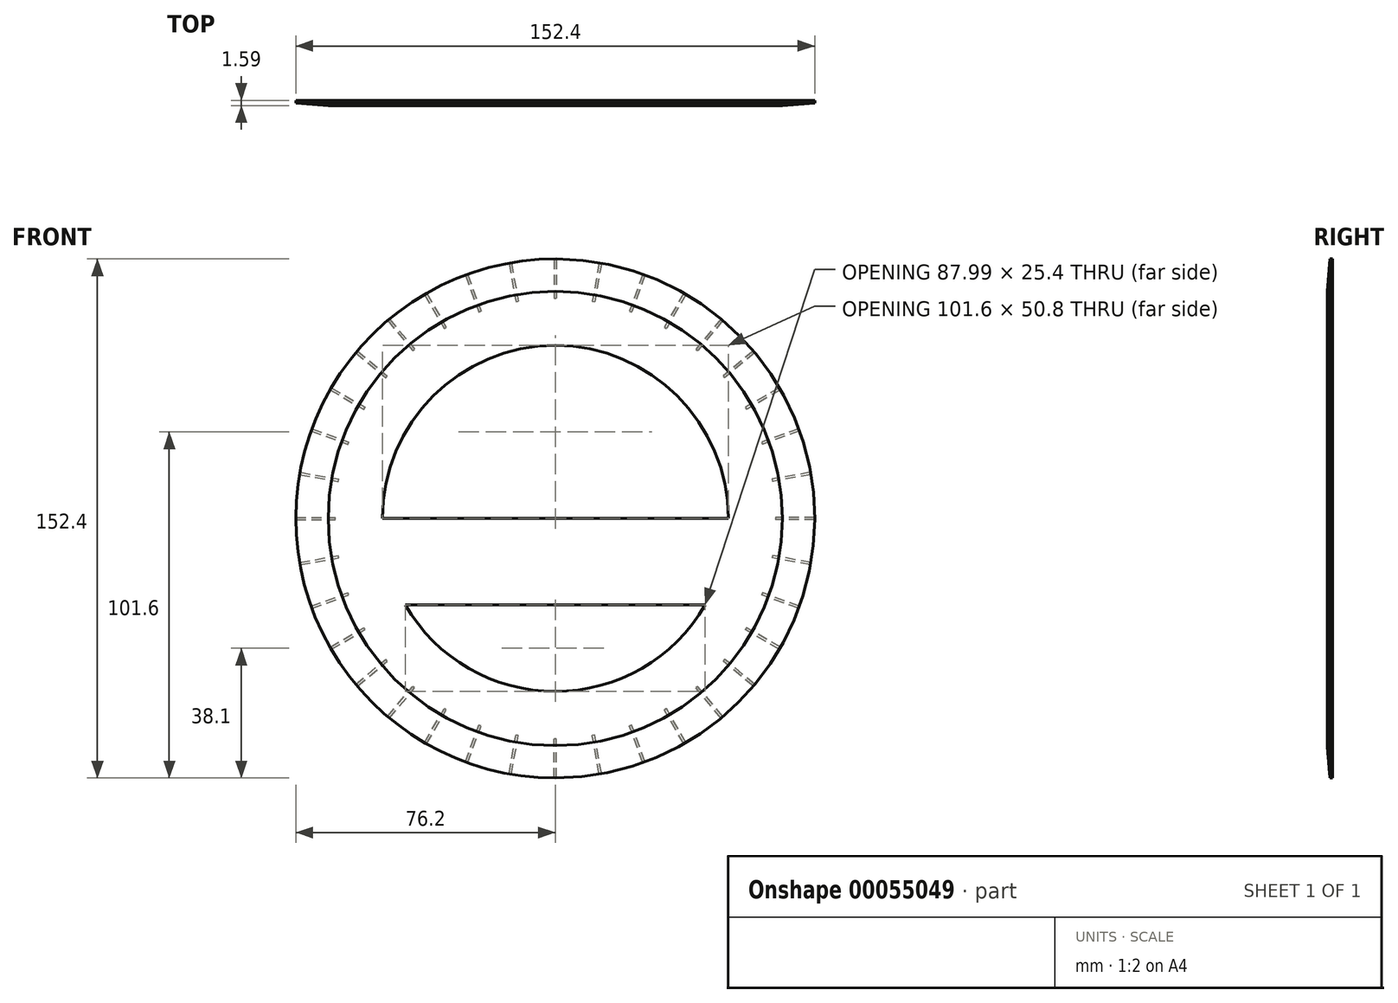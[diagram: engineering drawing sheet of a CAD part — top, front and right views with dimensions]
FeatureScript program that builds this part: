
annotation { "Feature Type Name" : "Feature", "Feature Type Description" : "" }
export const myFeature = defineFeature(function(context is Context, id is Id, definition is map)
    precondition{}
    {
        {
            var Q0;
            Q0=qCreatedBy(makeId("Front.planeOp"),FACE);
            var sketch = newSketch(context, id + "F0", { "sketchPlane" : qUnion([Q0])});
            skCircle(sketch, "E0", {"center": v(0, 0) * mm, "radius": 76.2 * mm});
            skCircle(sketch, "E1", {"center": v(0, 0) * mm, "radius": 50.8 * mm});
            skLineSegment(sketch, "E2", {"start": v(-50.8, 0) * mm, "end": v(50.8, 0) * mm});
            skLineSegment(sketch, "E3", {"start": v(-44, -25.4) * mm, "end": v(44, -25.4) * mm});
            skSolve(sketch);
        }
        {
            var Q0;
            Q0=makeQuery(id+"F0.imprint","IMPRINT",FACE,{"disambiguationData":[TD([[makeQuery(id+"F0.imprint","IMPRINT",EDGE,{"derivedFrom":sQuery(id+"F0.wireOp",EDGE,"E0")}),1.0]])]});
            var Q1;
            {var subQ0=sQuery(id+"F0.wireOp",EDGE,"E2");Q1=makeQuery(id+"F0.imprint","IMPRINT",FACE,{"disambiguationData":[TD([[makeQuery(id+"F0.imprint","IMPRINT",EDGE,{"derivedFrom":subQ0}),-1.0]])]});}
            extrude(context, id + "F1", {"entities" : qUnion([Q0, Q1]), "depth" : 1.59 * mm});
        }
        {
            var Q0;
            Q0=qCreatedBy(makeId("Top.planeOp"),FACE);
            var sketch = newSketch(context, id + "F2", { "sketchPlane" : qUnion([Q0])});
            skLineSegment(sketch, "E4", {"start": v(76.2, 0) * mm, "end": v(76.2, -1.59) * mm, "construction": true});
            skLineSegment(sketch, "E5.0", {"start": v(76.2, -1.59) * mm, "end": v(-76.2, -1.59) * mm, "construction": true});
            skLineSegment(sketch, "E6", {"start": v(76.2, -0.8) * mm, "end": v(66.67, -1.59) * mm});
            skLineSegment(sketch, "E7", {"start": v(66.67, -1.59) * mm, "end": v(76.2, -1.59) * mm});
            skLineSegment(sketch, "E8", {"start": v(0, 17.15) * mm, "end": v(0, -24.9) * mm, "construction": true});
            skLineSegment(sketch, "E9", {"start": v(76.2, -0.8) * mm, "end": v(76.2, -1.59) * mm});
            skSolve(sketch);
        }
        {
            var Q0;
            Q0=makeQuery(id+"F2.imprint","IMPRINT",FACE,{"disambiguationData":[TD([[makeQuery(id+"F2.imprint","IMPRINT",EDGE,{"derivedFrom":sQuery(id+"F2.wireOp",EDGE,"E6")}),1.0]])]});
            var Q1;
            Q1=sQuery(id+"F2.wireOp",EDGE,"E9");
            var Q2;
            Q2=sQuery(id+"F2.wireOp",EDGE,"E6");
            var Q3;
            Q3=sQuery(id+"F2.wireOp",EDGE,"E7");
            var Q4;
            Q4=sQuery(id+"F2.wireOp",EDGE,"E8");
            revolve(context, id + "F3", {"operationType" : NewBodyOperationType.REMOVE, "entities" : qUnion([Q0]), "surfaceEntities" : qUnion([Q1, Q2, Q3]), "axis" : qUnion([Q4]), "revolveType" : RevolveType.FULL, "oppositeDirection" : true});
        }
        {
            var Q0;
            Q0=makeQuery(id+"F1.opExtrude","CAP_FACE",FACE,{"disambiguationData":[OSD([sQuery(id+"F0.wireOp",EDGE,"E0"),sQuery(id+"F0.wireOp",EDGE,"E1"),sQuery(id+"F0.wireOp",EDGE,"E2"),sQuery(id+"F0.wireOp",EDGE,"E3")])],"isStart":true});
            var sketch = newSketch(context, id + "F4", { "sketchPlane" : qUnion([Q0])});
            skLineSegment(sketch, "E10.rect.bottom", {"start": v(76.2, -0.35) * mm, "end": v(64.66, -0.35) * mm});
            skLineSegment(sketch, "E10.rect.top", {"start": v(76.2, 0.35) * mm, "end": v(64.66, 0.35) * mm});
            skLineSegment(sketch, "E10.rect.left", {"start": v(76.2, -0.35) * mm, "end": v(76.2, 0.35) * mm});
            skLineSegment(sketch, "E10.rect.right", {"start": v(64.66, -0.35) * mm, "end": v(64.66, 0.35) * mm});
            skPoint(sketch, "E10.rect.middle", {"position": v(70.43, 0) * mm});
            skLineSegment(sketch, "E11.1.0", {"start": v(75.1, 12.9) * mm, "end": v(63.74, 10.89) * mm});
            skLineSegment(sketch, "E11.1.1", {"start": v(74.98, 13.57) * mm, "end": v(63.62, 11.57) * mm});
            skPoint(sketch, "E11.1.2", {"position": v(69.36, 12.23) * mm});
            skLineSegment(sketch, "E11.1.3", {"start": v(75.1, 12.9) * mm, "end": v(74.98, 13.57) * mm});
            skLineSegment(sketch, "E11.1.4", {"start": v(63.74, 10.89) * mm, "end": v(63.62, 11.57) * mm});
            skLineSegment(sketch, "E11.2.0", {"start": v(71.72, 25.74) * mm, "end": v(60.88, 21.8) * mm});
            skLineSegment(sketch, "E11.2.1", {"start": v(71.49, 26.39) * mm, "end": v(60.65, 22.44) * mm});
            skPoint(sketch, "E11.2.2", {"position": v(66.18, 24.09) * mm});
            skLineSegment(sketch, "E11.2.3", {"start": v(71.72, 25.74) * mm, "end": v(71.49, 26.39) * mm});
            skLineSegment(sketch, "E11.2.4", {"start": v(60.88, 21.8) * mm, "end": v(60.65, 22.44) * mm});
            skLineSegment(sketch, "E11.3.0", {"start": v(66.16, 37.8) * mm, "end": v(56.17, 32.03) * mm});
            skLineSegment(sketch, "E11.3.1", {"start": v(65.82, 38.4) * mm, "end": v(55.83, 32.63) * mm});
            skPoint(sketch, "E11.3.2", {"position": v(61, 35.22) * mm});
            skLineSegment(sketch, "E11.3.3", {"start": v(66.16, 37.8) * mm, "end": v(65.82, 38.4) * mm});
            skLineSegment(sketch, "E11.3.4", {"start": v(56.17, 32.03) * mm, "end": v(55.83, 32.63) * mm});
            skLineSegment(sketch, "E11.4.0", {"start": v(58.6, 48.71) * mm, "end": v(49.76, 41.3) * mm});
            skLineSegment(sketch, "E11.4.1", {"start": v(58.15, 49.25) * mm, "end": v(49.31, 41.83) * mm});
            skPoint(sketch, "E11.4.2", {"position": v(53.95, 45.27) * mm});
            skLineSegment(sketch, "E11.4.3", {"start": v(58.6, 48.71) * mm, "end": v(58.15, 49.25) * mm});
            skLineSegment(sketch, "E11.4.4", {"start": v(49.76, 41.3) * mm, "end": v(49.31, 41.83) * mm});
            skLineSegment(sketch, "E11.5.0", {"start": v(49.25, 58.15) * mm, "end": v(41.83, 49.31) * mm});
            skLineSegment(sketch, "E11.5.1", {"start": v(48.71, 58.6) * mm, "end": v(41.3, 49.76) * mm});
            skPoint(sketch, "E11.5.2", {"position": v(45.27, 53.95) * mm});
            skLineSegment(sketch, "E11.5.3", {"start": v(49.25, 58.15) * mm, "end": v(48.71, 58.6) * mm});
            skLineSegment(sketch, "E11.5.4", {"start": v(41.83, 49.31) * mm, "end": v(41.3, 49.76) * mm});
            skLineSegment(sketch, "E11.6.0", {"start": v(38.4, 65.82) * mm, "end": v(32.63, 55.83) * mm});
            skLineSegment(sketch, "E11.6.1", {"start": v(37.8, 66.16) * mm, "end": v(32.03, 56.17) * mm});
            skPoint(sketch, "E11.6.2", {"position": v(35.22, 61) * mm});
            skLineSegment(sketch, "E11.6.3", {"start": v(38.4, 65.82) * mm, "end": v(37.8, 66.16) * mm});
            skLineSegment(sketch, "E11.6.4", {"start": v(32.63, 55.83) * mm, "end": v(32.03, 56.17) * mm});
            skLineSegment(sketch, "E11.7.0", {"start": v(26.39, 71.49) * mm, "end": v(22.44, 60.65) * mm});
            skLineSegment(sketch, "E11.7.1", {"start": v(25.74, 71.72) * mm, "end": v(21.8, 60.88) * mm});
            skPoint(sketch, "E11.7.2", {"position": v(24.09, 66.18) * mm});
            skLineSegment(sketch, "E11.7.3", {"start": v(26.39, 71.49) * mm, "end": v(25.74, 71.72) * mm});
            skLineSegment(sketch, "E11.7.4", {"start": v(22.44, 60.65) * mm, "end": v(21.8, 60.88) * mm});
            skLineSegment(sketch, "E11.8.0", {"start": v(13.57, 74.98) * mm, "end": v(11.57, 63.62) * mm});
            skLineSegment(sketch, "E11.8.1", {"start": v(12.9, 75.1) * mm, "end": v(10.89, 63.74) * mm});
            skPoint(sketch, "E11.8.2", {"position": v(12.23, 69.36) * mm});
            skLineSegment(sketch, "E11.8.3", {"start": v(13.57, 74.98) * mm, "end": v(12.9, 75.1) * mm});
            skLineSegment(sketch, "E11.8.4", {"start": v(11.57, 63.62) * mm, "end": v(10.89, 63.74) * mm});
            skLineSegment(sketch, "E11.9.0", {"start": v(0.35, 76.2) * mm, "end": v(0.35, 64.66) * mm});
            skLineSegment(sketch, "E11.9.1", {"start": v(-0.35, 76.2) * mm, "end": v(-0.35, 64.66) * mm});
            skPoint(sketch, "E11.9.2", {"position": v(0, 70.43) * mm});
            skLineSegment(sketch, "E11.9.3", {"start": v(0.35, 76.2) * mm, "end": v(-0.35, 76.2) * mm});
            skLineSegment(sketch, "E11.9.4", {"start": v(0.35, 64.66) * mm, "end": v(-0.35, 64.66) * mm});
            skLineSegment(sketch, "E11.10.0", {"start": v(-12.9, 75.1) * mm, "end": v(-10.89, 63.74) * mm});
            skLineSegment(sketch, "E11.10.1", {"start": v(-13.57, 74.98) * mm, "end": v(-11.57, 63.62) * mm});
            skPoint(sketch, "E11.10.2", {"position": v(-12.23, 69.36) * mm});
            skLineSegment(sketch, "E11.10.3", {"start": v(-12.9, 75.1) * mm, "end": v(-13.57, 74.98) * mm});
            skLineSegment(sketch, "E11.10.4", {"start": v(-10.89, 63.74) * mm, "end": v(-11.57, 63.62) * mm});
            skLineSegment(sketch, "E11.11.0", {"start": v(-25.74, 71.72) * mm, "end": v(-21.8, 60.88) * mm});
            skLineSegment(sketch, "E11.11.1", {"start": v(-26.39, 71.49) * mm, "end": v(-22.44, 60.65) * mm});
            skPoint(sketch, "E11.11.2", {"position": v(-24.09, 66.18) * mm});
            skLineSegment(sketch, "E11.11.3", {"start": v(-25.74, 71.72) * mm, "end": v(-26.39, 71.49) * mm});
            skLineSegment(sketch, "E11.11.4", {"start": v(-21.8, 60.88) * mm, "end": v(-22.44, 60.65) * mm});
            skLineSegment(sketch, "E11.12.0", {"start": v(-37.8, 66.16) * mm, "end": v(-32.03, 56.17) * mm});
            skLineSegment(sketch, "E11.12.1", {"start": v(-38.4, 65.82) * mm, "end": v(-32.63, 55.83) * mm});
            skPoint(sketch, "E11.12.2", {"position": v(-35.22, 61) * mm});
            skLineSegment(sketch, "E11.12.3", {"start": v(-37.8, 66.16) * mm, "end": v(-38.4, 65.82) * mm});
            skLineSegment(sketch, "E11.12.4", {"start": v(-32.03, 56.17) * mm, "end": v(-32.63, 55.83) * mm});
            skLineSegment(sketch, "E11.13.0", {"start": v(-48.71, 58.6) * mm, "end": v(-41.3, 49.76) * mm});
            skLineSegment(sketch, "E11.13.1", {"start": v(-49.25, 58.15) * mm, "end": v(-41.83, 49.31) * mm});
            skPoint(sketch, "E11.13.2", {"position": v(-45.27, 53.95) * mm});
            skLineSegment(sketch, "E11.13.3", {"start": v(-48.71, 58.6) * mm, "end": v(-49.25, 58.15) * mm});
            skLineSegment(sketch, "E11.13.4", {"start": v(-41.3, 49.76) * mm, "end": v(-41.83, 49.31) * mm});
            skLineSegment(sketch, "E11.14.0", {"start": v(-58.15, 49.25) * mm, "end": v(-49.31, 41.83) * mm});
            skLineSegment(sketch, "E11.14.1", {"start": v(-58.6, 48.71) * mm, "end": v(-49.76, 41.3) * mm});
            skPoint(sketch, "E11.14.2", {"position": v(-53.95, 45.27) * mm});
            skLineSegment(sketch, "E11.14.3", {"start": v(-58.15, 49.25) * mm, "end": v(-58.6, 48.71) * mm});
            skLineSegment(sketch, "E11.14.4", {"start": v(-49.31, 41.83) * mm, "end": v(-49.76, 41.3) * mm});
            skLineSegment(sketch, "E11.15.0", {"start": v(-65.82, 38.4) * mm, "end": v(-55.83, 32.63) * mm});
            skLineSegment(sketch, "E11.15.1", {"start": v(-66.16, 37.8) * mm, "end": v(-56.17, 32.03) * mm});
            skPoint(sketch, "E11.15.2", {"position": v(-61, 35.22) * mm});
            skLineSegment(sketch, "E11.15.3", {"start": v(-65.82, 38.4) * mm, "end": v(-66.16, 37.8) * mm});
            skLineSegment(sketch, "E11.15.4", {"start": v(-55.83, 32.63) * mm, "end": v(-56.17, 32.03) * mm});
            skLineSegment(sketch, "E11.16.0", {"start": v(-71.49, 26.39) * mm, "end": v(-60.65, 22.44) * mm});
            skLineSegment(sketch, "E11.16.1", {"start": v(-71.72, 25.74) * mm, "end": v(-60.88, 21.8) * mm});
            skPoint(sketch, "E11.16.2", {"position": v(-66.18, 24.09) * mm});
            skLineSegment(sketch, "E11.16.3", {"start": v(-71.49, 26.39) * mm, "end": v(-71.72, 25.74) * mm});
            skLineSegment(sketch, "E11.16.4", {"start": v(-60.65, 22.44) * mm, "end": v(-60.88, 21.8) * mm});
            skLineSegment(sketch, "E11.17.0", {"start": v(-74.98, 13.57) * mm, "end": v(-63.62, 11.57) * mm});
            skLineSegment(sketch, "E11.17.1", {"start": v(-75.1, 12.9) * mm, "end": v(-63.74, 10.89) * mm});
            skPoint(sketch, "E11.17.2", {"position": v(-69.36, 12.23) * mm});
            skLineSegment(sketch, "E11.17.3", {"start": v(-74.98, 13.57) * mm, "end": v(-75.1, 12.9) * mm});
            skLineSegment(sketch, "E11.17.4", {"start": v(-63.62, 11.57) * mm, "end": v(-63.74, 10.89) * mm});
            skLineSegment(sketch, "E11.18.0", {"start": v(-76.2, 0.35) * mm, "end": v(-64.66, 0.35) * mm});
            skLineSegment(sketch, "E11.18.1", {"start": v(-76.2, -0.35) * mm, "end": v(-64.66, -0.35) * mm});
            skPoint(sketch, "E11.18.2", {"position": v(-70.43, 0) * mm});
            skLineSegment(sketch, "E11.18.3", {"start": v(-76.2, 0.35) * mm, "end": v(-76.2, -0.35) * mm});
            skLineSegment(sketch, "E11.18.4", {"start": v(-64.66, 0.35) * mm, "end": v(-64.66, -0.35) * mm});
            skLineSegment(sketch, "E11.19.0", {"start": v(-75.1, -12.9) * mm, "end": v(-63.74, -10.89) * mm});
            skLineSegment(sketch, "E11.19.1", {"start": v(-74.98, -13.57) * mm, "end": v(-63.62, -11.57) * mm});
            skPoint(sketch, "E11.19.2", {"position": v(-69.36, -12.23) * mm});
            skLineSegment(sketch, "E11.19.3", {"start": v(-75.1, -12.9) * mm, "end": v(-74.98, -13.57) * mm});
            skLineSegment(sketch, "E11.19.4", {"start": v(-63.74, -10.89) * mm, "end": v(-63.62, -11.57) * mm});
            skLineSegment(sketch, "E11.20.0", {"start": v(-71.72, -25.74) * mm, "end": v(-60.88, -21.8) * mm});
            skLineSegment(sketch, "E11.20.1", {"start": v(-71.49, -26.39) * mm, "end": v(-60.65, -22.44) * mm});
            skPoint(sketch, "E11.20.2", {"position": v(-66.18, -24.09) * mm});
            skLineSegment(sketch, "E11.20.3", {"start": v(-71.72, -25.74) * mm, "end": v(-71.49, -26.39) * mm});
            skLineSegment(sketch, "E11.20.4", {"start": v(-60.88, -21.8) * mm, "end": v(-60.65, -22.44) * mm});
            skLineSegment(sketch, "E11.21.0", {"start": v(-66.16, -37.8) * mm, "end": v(-56.17, -32.03) * mm});
            skLineSegment(sketch, "E11.21.1", {"start": v(-65.82, -38.4) * mm, "end": v(-55.83, -32.63) * mm});
            skPoint(sketch, "E11.21.2", {"position": v(-61, -35.22) * mm});
            skLineSegment(sketch, "E11.21.3", {"start": v(-66.16, -37.8) * mm, "end": v(-65.82, -38.4) * mm});
            skLineSegment(sketch, "E11.21.4", {"start": v(-56.17, -32.03) * mm, "end": v(-55.83, -32.63) * mm});
            skLineSegment(sketch, "E11.22.0", {"start": v(-58.6, -48.71) * mm, "end": v(-49.76, -41.3) * mm});
            skLineSegment(sketch, "E11.22.1", {"start": v(-58.15, -49.25) * mm, "end": v(-49.31, -41.83) * mm});
            skPoint(sketch, "E11.22.2", {"position": v(-53.95, -45.27) * mm});
            skLineSegment(sketch, "E11.22.3", {"start": v(-58.6, -48.71) * mm, "end": v(-58.15, -49.25) * mm});
            skLineSegment(sketch, "E11.22.4", {"start": v(-49.76, -41.3) * mm, "end": v(-49.31, -41.83) * mm});
            skLineSegment(sketch, "E11.23.0", {"start": v(-49.25, -58.15) * mm, "end": v(-41.83, -49.31) * mm});
            skLineSegment(sketch, "E11.23.1", {"start": v(-48.71, -58.6) * mm, "end": v(-41.3, -49.76) * mm});
            skPoint(sketch, "E11.23.2", {"position": v(-45.27, -53.95) * mm});
            skLineSegment(sketch, "E11.23.3", {"start": v(-49.25, -58.15) * mm, "end": v(-48.71, -58.6) * mm});
            skLineSegment(sketch, "E11.23.4", {"start": v(-41.83, -49.31) * mm, "end": v(-41.3, -49.76) * mm});
            skLineSegment(sketch, "E11.24.0", {"start": v(-38.4, -65.82) * mm, "end": v(-32.63, -55.83) * mm});
            skLineSegment(sketch, "E11.24.1", {"start": v(-37.8, -66.16) * mm, "end": v(-32.03, -56.17) * mm});
            skPoint(sketch, "E11.24.2", {"position": v(-35.22, -61) * mm});
            skLineSegment(sketch, "E11.24.3", {"start": v(-38.4, -65.82) * mm, "end": v(-37.8, -66.16) * mm});
            skLineSegment(sketch, "E11.24.4", {"start": v(-32.63, -55.83) * mm, "end": v(-32.03, -56.17) * mm});
            skLineSegment(sketch, "E11.25.0", {"start": v(-26.39, -71.49) * mm, "end": v(-22.44, -60.65) * mm});
            skLineSegment(sketch, "E11.25.1", {"start": v(-25.74, -71.72) * mm, "end": v(-21.8, -60.88) * mm});
            skPoint(sketch, "E11.25.2", {"position": v(-24.09, -66.18) * mm});
            skLineSegment(sketch, "E11.25.3", {"start": v(-26.39, -71.49) * mm, "end": v(-25.74, -71.72) * mm});
            skLineSegment(sketch, "E11.25.4", {"start": v(-22.44, -60.65) * mm, "end": v(-21.8, -60.88) * mm});
            skLineSegment(sketch, "E11.26.0", {"start": v(-13.57, -74.98) * mm, "end": v(-11.57, -63.62) * mm});
            skLineSegment(sketch, "E11.26.1", {"start": v(-12.9, -75.1) * mm, "end": v(-10.89, -63.74) * mm});
            skPoint(sketch, "E11.26.2", {"position": v(-12.23, -69.36) * mm});
            skLineSegment(sketch, "E11.26.3", {"start": v(-13.57, -74.98) * mm, "end": v(-12.9, -75.1) * mm});
            skLineSegment(sketch, "E11.26.4", {"start": v(-11.57, -63.62) * mm, "end": v(-10.89, -63.74) * mm});
            skLineSegment(sketch, "E11.27.0", {"start": v(-0.35, -76.2) * mm, "end": v(-0.35, -64.66) * mm});
            skLineSegment(sketch, "E11.27.1", {"start": v(0.35, -76.2) * mm, "end": v(0.35, -64.66) * mm});
            skPoint(sketch, "E11.27.2", {"position": v(0, -70.43) * mm});
            skLineSegment(sketch, "E11.27.3", {"start": v(-0.35, -76.2) * mm, "end": v(0.35, -76.2) * mm});
            skLineSegment(sketch, "E11.27.4", {"start": v(-0.35, -64.66) * mm, "end": v(0.35, -64.66) * mm});
            skLineSegment(sketch, "E11.28.0", {"start": v(12.9, -75.1) * mm, "end": v(10.89, -63.74) * mm});
            skLineSegment(sketch, "E11.28.1", {"start": v(13.57, -74.98) * mm, "end": v(11.57, -63.62) * mm});
            skPoint(sketch, "E11.28.2", {"position": v(12.23, -69.36) * mm});
            skLineSegment(sketch, "E11.28.3", {"start": v(12.9, -75.1) * mm, "end": v(13.57, -74.98) * mm});
            skLineSegment(sketch, "E11.28.4", {"start": v(10.89, -63.74) * mm, "end": v(11.57, -63.62) * mm});
            skLineSegment(sketch, "E11.29.0", {"start": v(25.74, -71.72) * mm, "end": v(21.8, -60.88) * mm});
            skLineSegment(sketch, "E11.29.1", {"start": v(26.39, -71.49) * mm, "end": v(22.44, -60.65) * mm});
            skPoint(sketch, "E11.29.2", {"position": v(24.09, -66.18) * mm});
            skLineSegment(sketch, "E11.29.3", {"start": v(25.74, -71.72) * mm, "end": v(26.39, -71.49) * mm});
            skLineSegment(sketch, "E11.29.4", {"start": v(21.8, -60.88) * mm, "end": v(22.44, -60.65) * mm});
            skLineSegment(sketch, "E11.30.0", {"start": v(37.8, -66.16) * mm, "end": v(32.03, -56.17) * mm});
            skLineSegment(sketch, "E11.30.1", {"start": v(38.4, -65.82) * mm, "end": v(32.63, -55.83) * mm});
            skPoint(sketch, "E11.30.2", {"position": v(35.22, -61) * mm});
            skLineSegment(sketch, "E11.30.3", {"start": v(37.8, -66.16) * mm, "end": v(38.4, -65.82) * mm});
            skLineSegment(sketch, "E11.30.4", {"start": v(32.03, -56.17) * mm, "end": v(32.63, -55.83) * mm});
            skLineSegment(sketch, "E11.31.0", {"start": v(48.71, -58.6) * mm, "end": v(41.3, -49.76) * mm});
            skLineSegment(sketch, "E11.31.1", {"start": v(49.25, -58.15) * mm, "end": v(41.83, -49.31) * mm});
            skPoint(sketch, "E11.31.2", {"position": v(45.27, -53.95) * mm});
            skLineSegment(sketch, "E11.31.3", {"start": v(48.71, -58.6) * mm, "end": v(49.25, -58.15) * mm});
            skLineSegment(sketch, "E11.31.4", {"start": v(41.3, -49.76) * mm, "end": v(41.83, -49.31) * mm});
            skLineSegment(sketch, "E11.32.0", {"start": v(58.15, -49.25) * mm, "end": v(49.31, -41.83) * mm});
            skLineSegment(sketch, "E11.32.1", {"start": v(58.6, -48.71) * mm, "end": v(49.76, -41.3) * mm});
            skPoint(sketch, "E11.32.2", {"position": v(53.95, -45.27) * mm});
            skLineSegment(sketch, "E11.32.3", {"start": v(58.15, -49.25) * mm, "end": v(58.6, -48.71) * mm});
            skLineSegment(sketch, "E11.32.4", {"start": v(49.31, -41.83) * mm, "end": v(49.76, -41.3) * mm});
            skLineSegment(sketch, "E11.33.0", {"start": v(65.82, -38.4) * mm, "end": v(55.83, -32.63) * mm});
            skLineSegment(sketch, "E11.33.1", {"start": v(66.16, -37.8) * mm, "end": v(56.17, -32.03) * mm});
            skPoint(sketch, "E11.33.2", {"position": v(61, -35.22) * mm});
            skLineSegment(sketch, "E11.33.3", {"start": v(65.82, -38.4) * mm, "end": v(66.16, -37.8) * mm});
            skLineSegment(sketch, "E11.33.4", {"start": v(55.83, -32.63) * mm, "end": v(56.17, -32.03) * mm});
            skLineSegment(sketch, "E11.34.0", {"start": v(71.49, -26.39) * mm, "end": v(60.65, -22.44) * mm});
            skLineSegment(sketch, "E11.34.1", {"start": v(71.72, -25.74) * mm, "end": v(60.88, -21.8) * mm});
            skPoint(sketch, "E11.34.2", {"position": v(66.18, -24.09) * mm});
            skLineSegment(sketch, "E11.34.3", {"start": v(71.49, -26.39) * mm, "end": v(71.72, -25.74) * mm});
            skLineSegment(sketch, "E11.34.4", {"start": v(60.65, -22.44) * mm, "end": v(60.88, -21.8) * mm});
            skLineSegment(sketch, "E11.35.0", {"start": v(74.98, -13.57) * mm, "end": v(63.62, -11.57) * mm});
            skLineSegment(sketch, "E11.35.1", {"start": v(75.1, -12.9) * mm, "end": v(63.74, -10.89) * mm});
            skPoint(sketch, "E11.35.2", {"position": v(69.36, -12.23) * mm});
            skLineSegment(sketch, "E11.35.3", {"start": v(74.98, -13.57) * mm, "end": v(75.1, -12.9) * mm});
            skLineSegment(sketch, "E11.35.4", {"start": v(63.62, -11.57) * mm, "end": v(63.74, -10.89) * mm});
            skPoint(sketch, "E11.center", {"position": v(0, 0) * mm});
            skSolve(sketch);
        }
        {
            var Q0;
            Q0 = qSketchRegion(id + "F4", true);
            extrude(context, id + "F5", {"entities" : qUnion([Q0]), "operationType" : NewBodyOperationType.REMOVE, "oppositeDirection" : true, "depth" : 0.03 * mm});
        }
    });
